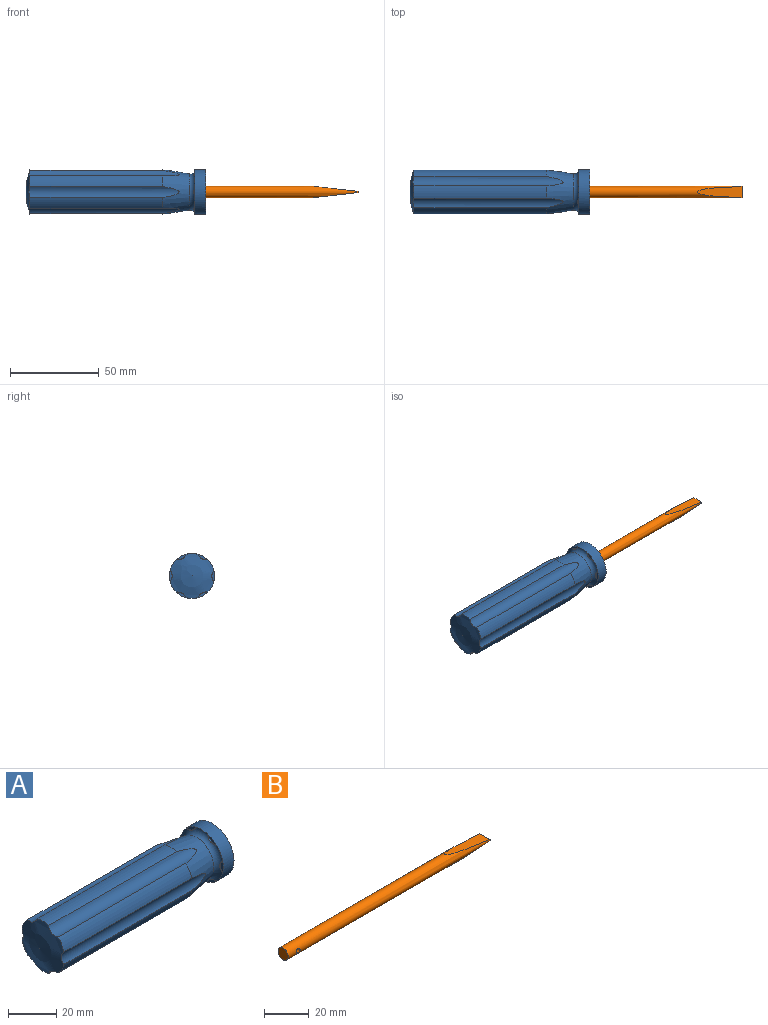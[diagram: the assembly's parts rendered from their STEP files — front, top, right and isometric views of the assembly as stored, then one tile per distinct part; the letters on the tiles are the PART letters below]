
ASSEMBLY  parts=2 mates=1
PART A: 31 faces, bbox 101.6x31.4x31.4 mm
  f0: cylinder r=12.7mm len=75.04mm, axis (1,0,0), area 526.2mm2, adj f6,f10,f13,f18
  f1: cylinder r=12.7mm len=75.04mm, axis (1,0,0), area 526.2mm2, adj f6,f10,f17,f18
  f2: cylinder r=12.7mm len=75.04mm, axis (1,0,0), area 526.2mm2, adj f6,f10,f16,f17
  f3: cylinder r=12.7mm len=75.04mm, axis (1,0,0), area 526.2mm2, adj f6,f10,f15,f16
  f4: cylinder r=12.7mm len=75.04mm, axis (1,0,0), area 526.2mm2, adj f6,f10,f14,f15
  f5: cylinder r=12.7mm len=75.04mm, axis (1,0,0), area 526.2mm2, adj f6,f10,f13,f14
  f6: sphere r=38.1mm, area 480.8mm2, adj f0,f1,f2,f3,f4,f5,f13,f14
  f7: plane 25.4x25.4mm, normal (1,0,0), area 475mm2, adj f8,f11
  f8: cylinder r=12.7mm len=25.4mm, axis (1,0,0), area 506.7mm2, adj f7,f9,f20,f22,f24,f26,f28,f30
  f9: torus R=12.7mm, axis (1,0,0), area 264mm2, adj f8,f10,f19,f21,f23,f25,f27,f29
  f10: cone r=12.7mm half-angle=9.4deg, axis (-1,0,0), area 863.7mm2, adj f0,f1,f2,f3,f4,f5,f9,f13
  f11: cylinder r=3.17mm len=41.15mm, axis (1,0,0), area 820.9mm2, adj f7,f12
  f12: plane 6.35x6.35mm, normal (1,0,0), area 31.7mm2, adj f11
  f13: cylinder r=4.83mm len=84.71mm, axis (1,0,0), area 550.2mm2, adj f0,f5,f6,f10
  f14: cylinder r=4.83mm len=84.71mm, axis (1,0,0), area 550.2mm2, adj f4,f5,f6,f10
  f15: cylinder r=4.83mm len=84.71mm, axis (1,0,0), area 550.2mm2, adj f3,f4,f6,f10
  f16: cylinder r=4.83mm len=84.71mm, axis (1,0,0), area 550.2mm2, adj f2,f3,f6,f10
  f17: cylinder r=4.83mm len=84.71mm, axis (1,0,0), area 550.2mm2, adj f1,f2,f6,f10
  f18: cylinder r=4.83mm len=84.71mm, axis (1,0,0), area 550.2mm2, adj f0,f1,f6,f10
  f19: cylinder r=4.83mm len=5.39mm, axis (1,0,0), area 1.7mm2, adj f9,f20
  f20: plane 5.39x3.19mm, normal (-1,0,0), area 6.5mm2, adj f8,f19
  f21: cylinder r=4.83mm len=6.22mm, axis (1,0,0), area 1.7mm2, adj f9,f22
  f22: plane 6.22x1.52mm, normal (-1,0,0), area 6.5mm2, adj f8,f21
  f23: cylinder r=4.83mm len=5.39mm, axis (1,0,0), area 1.7mm2, adj f9,f24
  f24: plane 5.39x3.19mm, normal (-1,0,0), area 6.5mm2, adj f8,f23
  f25: cylinder r=4.83mm len=5.39mm, axis (1,0,0), area 1.7mm2, adj f9,f26
  f26: plane 5.39x3.19mm, normal (-1,0,0), area 6.5mm2, adj f8,f25
  f27: cylinder r=4.83mm len=6.22mm, axis (1,0,0), area 1.7mm2, adj f9,f28
  f28: plane 6.22x1.52mm, normal (-1,0,0), area 6.5mm2, adj f8,f27
  f29: cylinder r=4.83mm len=5.39mm, axis (1,0,0), area 1.7mm2, adj f9,f30
  f30: plane 5.39x3.19mm, normal (-1,0,0), area 6.5mm2, adj f8,f29
PART B: 6 faces, bbox 127x6.4x6.4 mm
  f0: cylinder r=3.17mm len=127mm, axis (1,0,0), area 2224.1mm2, adj f1,f2,f3,f4,f5
  f1: plane 6.35x0.76mm, normal (1,0,0), area 4.8mm2, adj f0,f3,f4
  f2: plane 6.35x6.35mm, normal (-1,0,0), area 31.7mm2, adj f0
  f3: plane 25.4x6.3mm, normal (0.11,0,0.99), area 122.7mm2, adj f0,f1
  f4: plane 25.4x6.3mm, normal (0.11,0,-0.99), area 122.7mm2, adj f0,f1
  f5: cylinder r=1.21mm len=6.35mm, axis (0,-1,0), area 46.3mm2, adj f0
PLACE A t=(86.07,49.46,-19.7)mm
PLACE B t=(171.92,49.46,-19.7)mm
MATE fastened A.f0 <-> B.f0  axis (1,0,0) through (44.92,49.46,-19.7)mm
